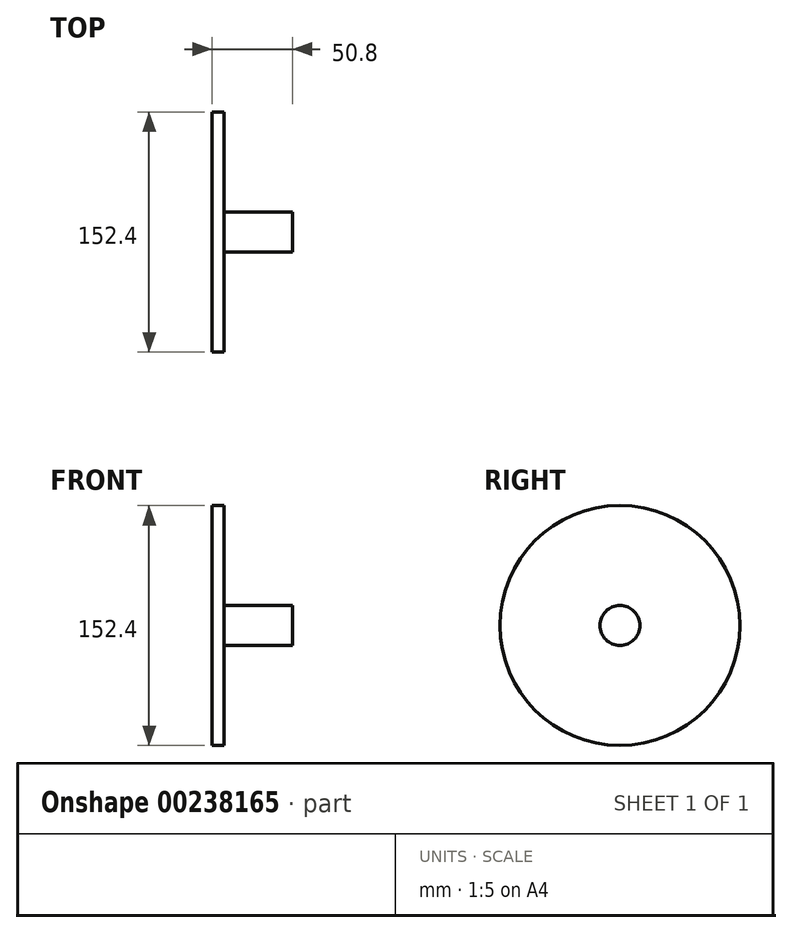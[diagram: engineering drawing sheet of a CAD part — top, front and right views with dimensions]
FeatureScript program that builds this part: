
annotation { "Feature Type Name" : "Feature", "Feature Type Description" : "" }
export const myFeature = defineFeature(function(context is Context, id is Id, definition is map)
    precondition{}
    {
        {
            var Q0;
            Q0=qCreatedBy(makeId("Front.planeOp"),FACE);
            var sketch = newSketch(context, id + "F0", { "sketchPlane" : qUnion([Q0])});
            skLineSegment(sketch, "E0", {"start": v(0, 0) * mm, "end": v(0, 76.2) * mm});
            skLineSegment(sketch, "E1", {"start": v(0, 76.2) * mm, "end": v(7.62, 76.2) * mm});
            skLineSegment(sketch, "E2", {"start": v(7.62, 76.2) * mm, "end": v(7.62, 12.7) * mm});
            skLineSegment(sketch, "E3", {"start": v(7.62, 12.7) * mm, "end": v(50.8, 12.7) * mm});
            skLineSegment(sketch, "E4", {"start": v(50.8, 12.7) * mm, "end": v(50.8, 0) * mm});
            skLineSegment(sketch, "E5", {"start": v(50.8, 0) * mm, "end": v(0, 0) * mm});
            skSolve(sketch);
        }
        {
            var Q0;
            Q0 = qSketchRegion(id + "F0", true);
            var Q1;
            Q1=sQuery(id+"F0.wireOp",EDGE,"E5");
            revolve(context, id + "F1", {"entities" : qUnion([Q0]), "axis" : qUnion([Q1]), "revolveType" : RevolveType.FULL});
        }
    });
